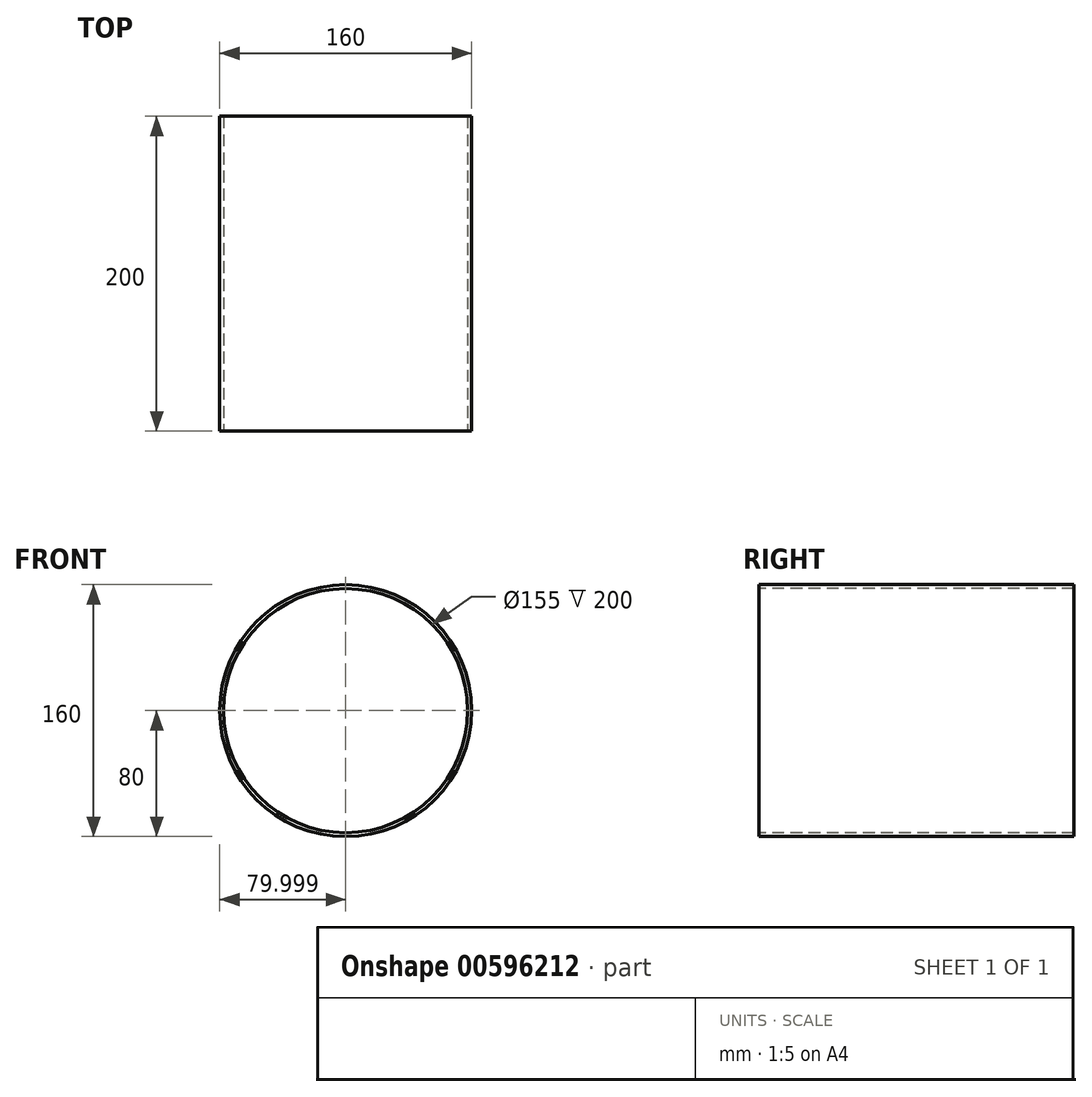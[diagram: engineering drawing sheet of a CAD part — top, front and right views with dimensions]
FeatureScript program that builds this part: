
annotation { "Feature Type Name" : "Feature", "Feature Type Description" : "" }
export const myFeature = defineFeature(function(context is Context, id is Id, definition is map)
    precondition{}
    {
        {
            var Q0;
            Q0=qCreatedBy(makeId("Front.planeOp"),FACE);
            var sketch = newSketch(context, id + "F0", { "sketchPlane" : qUnion([Q0])});
            skCircle(sketch, "E0", {"center": v(3.7, 0) * mm, "radius": 80 * mm});
            skSolve(sketch);
        }
        {
            var Q0;
            Q0=makeQuery(id+"F0.imprint","IMPRINT",FACE,{"disambiguationData":[TD([[makeQuery(id+"F0.imprint","IMPRINT",EDGE,{"derivedFrom":sQuery(id+"F0.wireOp",EDGE,"E0")}),1.0]])]});
            extrude(context, id + "F1", {"entities" : qUnion([Q0]), "oppositeDirection" : true, "depth" : 200 * mm, "offsetDistance" : 25 * mm});
        }
        {
            var Q0;
            Q0=makeQuery(id+"F1.opExtrude","CAP_FACE",FACE,{"disambiguationData":[OSD([sQuery(id+"F0.wireOp",EDGE,"E0")])],"isStart":true});
            var Q1;
            Q1=makeQuery(id+"F1.opExtrude","CAP_FACE",FACE,{"disambiguationData":[OSD([sQuery(id+"F0.wireOp",EDGE,"E0")])],"isStart":false});
            shell(context, id + "F2", {"entities" : qUnion([Q0, Q1]), "thickness" : 2.5 * mm});
        }
    });
